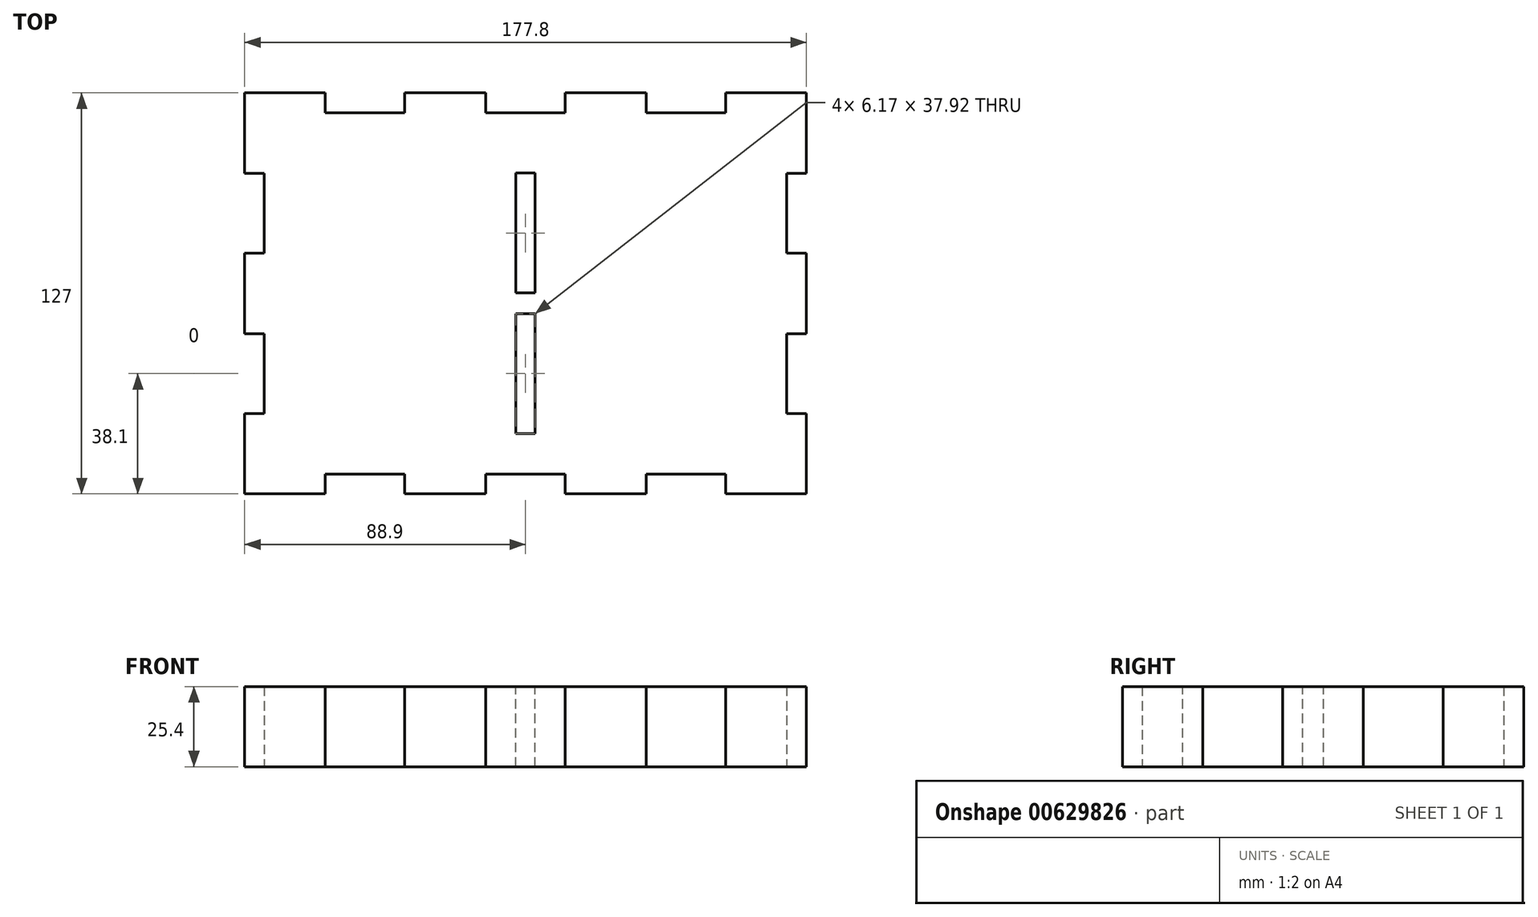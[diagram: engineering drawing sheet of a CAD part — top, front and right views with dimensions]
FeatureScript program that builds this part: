
annotation { "Feature Type Name" : "Feature", "Feature Type Description" : "" }
export const myFeature = defineFeature(function(context is Context, id is Id, definition is map)
    precondition{}
    {
        {
            var Q0;
            Q0=qCreatedBy(makeId("Top.planeOp"),FACE);
            var sketch = newSketch(context, id + "F0", { "sketchPlane" : qUnion([Q0])});
            skLineSegment(sketch, "E0.bottom", {"start": v(0, 0) * mm, "end": v(177.8, 0) * mm});
            skLineSegment(sketch, "E0.top", {"start": v(0, 127) * mm, "end": v(177.8, 127) * mm});
            skLineSegment(sketch, "E0.left", {"start": v(0, 0) * mm, "end": v(0, 127) * mm});
            skLineSegment(sketch, "E0.right", {"start": v(177.8, 0) * mm, "end": v(177.8, 127) * mm});
            skLineSegment(sketch, "E1.bottom", {"start": v(25.49, 0) * mm, "end": v(50.71, 0) * mm});
            skLineSegment(sketch, "E1.top", {"start": v(25.49, 6.26) * mm, "end": v(50.71, 6.26) * mm});
            skLineSegment(sketch, "E1.left", {"start": v(25.49, 0) * mm, "end": v(25.49, 6.26) * mm});
            skLineSegment(sketch, "E1.right", {"start": v(50.71, 0) * mm, "end": v(50.71, 6.26) * mm});
            skPoint(sketch, "E2", {"position": v(38.1, 6.26) * mm});
            skLineSegment(sketch, "E3.bottom", {"start": v(76.29, 6.26) * mm, "end": v(101.51, 6.26) * mm});
            skLineSegment(sketch, "E3.top", {"start": v(76.29, 0) * mm, "end": v(101.51, 0) * mm});
            skLineSegment(sketch, "E3.left", {"start": v(76.29, 6.26) * mm, "end": v(76.29, 0) * mm});
            skLineSegment(sketch, "E3.right", {"start": v(101.51, 6.26) * mm, "end": v(101.51, 0) * mm});
            skPoint(sketch, "E4", {"position": v(88.9, 6.26) * mm});
            skLineSegment(sketch, "E5.bottom", {"start": v(127.09, 6.26) * mm, "end": v(152.31, 6.26) * mm});
            skLineSegment(sketch, "E5.top", {"start": v(127.09, 0) * mm, "end": v(152.31, 0) * mm});
            skLineSegment(sketch, "E5.left", {"start": v(127.09, 6.26) * mm, "end": v(127.09, 0) * mm});
            skLineSegment(sketch, "E5.right", {"start": v(152.31, 6.26) * mm, "end": v(152.31, 0) * mm});
            skPoint(sketch, "E6", {"position": v(139.7, 6.26) * mm});
            skLineSegment(sketch, "E7.bottom", {"start": v(177.8, 25.49) * mm, "end": v(171.54, 25.49) * mm});
            skLineSegment(sketch, "E7.top", {"start": v(177.8, 50.71) * mm, "end": v(171.54, 50.71) * mm});
            skLineSegment(sketch, "E7.left", {"start": v(177.8, 25.49) * mm, "end": v(177.8, 50.71) * mm});
            skLineSegment(sketch, "E7.right", {"start": v(171.54, 25.49) * mm, "end": v(171.54, 50.71) * mm});
            skPoint(sketch, "E8", {"position": v(171.54, 38.1) * mm});
            skLineSegment(sketch, "E9.bottom", {"start": v(177.8, 101.51) * mm, "end": v(171.54, 101.51) * mm});
            skLineSegment(sketch, "E9.top", {"start": v(177.8, 76.29) * mm, "end": v(171.54, 76.29) * mm});
            skLineSegment(sketch, "E9.left", {"start": v(177.8, 101.51) * mm, "end": v(177.8, 76.29) * mm});
            skLineSegment(sketch, "E9.right", {"start": v(171.54, 101.51) * mm, "end": v(171.54, 76.29) * mm});
            skPoint(sketch, "E10", {"position": v(171.54, 88.9) * mm});
            skLineSegment(sketch, "E11", {"start": v(0, 63.5) * mm, "end": v(177.8, 63.5) * mm, "construction": true});
            skLineSegment(sketch, "E12.MirrorCS", {"start": v(25.49, 120.74) * mm, "end": v(50.71, 120.74) * mm});
            skLineSegment(sketch, "E13.MirrorCS", {"start": v(25.49, 127) * mm, "end": v(25.49, 120.74) * mm});
            skLineSegment(sketch, "E14.MirrorCS", {"start": v(50.71, 127) * mm, "end": v(50.71, 120.74) * mm});
            skLineSegment(sketch, "E15.MirrorCS", {"start": v(76.29, 120.74) * mm, "end": v(101.51, 120.74) * mm});
            skLineSegment(sketch, "E16.MirrorCS", {"start": v(76.29, 120.74) * mm, "end": v(76.29, 127) * mm});
            skLineSegment(sketch, "E17.MirrorCS", {"start": v(101.51, 120.74) * mm, "end": v(101.51, 127) * mm});
            skLineSegment(sketch, "E18.MirrorCS", {"start": v(127.09, 120.74) * mm, "end": v(127.09, 127) * mm});
            skLineSegment(sketch, "E19.MirrorCS", {"start": v(127.09, 120.74) * mm, "end": v(152.31, 120.74) * mm});
            skLineSegment(sketch, "E20.MirrorCS", {"start": v(152.31, 120.74) * mm, "end": v(152.31, 127) * mm});
            skLineSegment(sketch, "E21", {"start": v(88.9, 127) * mm, "end": v(88.9, 0) * mm, "construction": true});
            skLineSegment(sketch, "E22.MirrorCS", {"start": v(0, 101.51) * mm, "end": v(6.26, 101.51) * mm});
            skLineSegment(sketch, "E23.MirrorCS", {"start": v(6.26, 101.51) * mm, "end": v(6.26, 76.29) * mm});
            skLineSegment(sketch, "E24.MirrorCS", {"start": v(0, 76.29) * mm, "end": v(6.26, 76.29) * mm});
            skLineSegment(sketch, "E25.MirrorCS", {"start": v(0, 50.71) * mm, "end": v(6.26, 50.71) * mm});
            skLineSegment(sketch, "E26.MirrorCS", {"start": v(6.26, 25.49) * mm, "end": v(6.26, 50.71) * mm});
            skLineSegment(sketch, "E27.MirrorCS", {"start": v(0, 25.49) * mm, "end": v(6.26, 25.49) * mm});
            skSolve(sketch);
        }
        {
            var Q0;
            Q0=makeQuery(id+"F0.imprint","IMPRINT",FACE,{"disambiguationData":[TD([[makeQuery(id+"F0.imprint","IMPRINT",EDGE,{"derivedFrom":sQuery(id+"F0.wireOp",EDGE,"E1.top")}),1.0]])]});
            extrude(context, id + "F1", {"entities" : qUnion([Q0]), "depth" : 25.4 * mm, "offsetDistance" : 25.4 * mm});
        }
        {
            var Q0;
            Q0=makeQuery(id+"F1.opExtrude","CAP_FACE",FACE,{"disambiguationData":[OSD([sQuery(id+"F0.wireOp",EDGE,"E0.bottom"),sQuery(id+"F0.wireOp",EDGE,"E0.top"),sQuery(id+"F0.wireOp",EDGE,"E0.left"),sQuery(id+"F0.wireOp",EDGE,"E0.right"),sQuery(id+"F0.wireOp",EDGE,"E1.top"),sQuery(id+"F0.wireOp",EDGE,"E1.left"),sQuery(id+"F0.wireOp",EDGE,"E1.right"),sQuery(id+"F0.wireOp",EDGE,"E3.bottom"),sQuery(id+"F0.wireOp",EDGE,"E3.left"),sQuery(id+"F0.wireOp",EDGE,"E3.right"),sQuery(id+"F0.wireOp",EDGE,"E5.bottom"),sQuery(id+"F0.wireOp",EDGE,"E5.left"),sQuery(id+"F0.wireOp",EDGE,"E5.right"),sQuery(id+"F0.wireOp",EDGE,"E7.bottom"),sQuery(id+"F0.wireOp",EDGE,"E7.top"),sQuery(id+"F0.wireOp",EDGE,"E7.right"),sQuery(id+"F0.wireOp",EDGE,"E9.bottom"),sQuery(id+"F0.wireOp",EDGE,"E9.top"),sQuery(id+"F0.wireOp",EDGE,"E9.right"),sQuery(id+"F0.wireOp",EDGE,"E12.MirrorCS"),sQuery(id+"F0.wireOp",EDGE,"E13.MirrorCS"),sQuery(id+"F0.wireOp",EDGE,"E14.MirrorCS"),sQuery(id+"F0.wireOp",EDGE,"E15.MirrorCS"),sQuery(id+"F0.wireOp",EDGE,"E16.MirrorCS"),sQuery(id+"F0.wireOp",EDGE,"E17.MirrorCS"),sQuery(id+"F0.wireOp",EDGE,"E18.MirrorCS"),sQuery(id+"F0.wireOp",EDGE,"E19.MirrorCS"),sQuery(id+"F0.wireOp",EDGE,"E20.MirrorCS"),sQuery(id+"F0.wireOp",EDGE,"E22.MirrorCS"),sQuery(id+"F0.wireOp",EDGE,"E23.MirrorCS"),sQuery(id+"F0.wireOp",EDGE,"E24.MirrorCS"),sQuery(id+"F0.wireOp",EDGE,"E25.MirrorCS"),sQuery(id+"F0.wireOp",EDGE,"E26.MirrorCS"),sQuery(id+"F0.wireOp",EDGE,"E27.MirrorCS")])],"isStart":false});
            var sketch = newSketch(context, id + "F2", { "sketchPlane" : qUnion([Q0])});
            skLineSegment(sketch, "E28.bottom", {"start": v(85.81, 101.6) * mm, "end": v(91.99, 101.6) * mm});
            skLineSegment(sketch, "E28.top", {"start": v(85.81, 63.68) * mm, "end": v(91.99, 63.68) * mm});
            skLineSegment(sketch, "E28.left", {"start": v(85.81, 101.6) * mm, "end": v(85.81, 63.68) * mm});
            skLineSegment(sketch, "E28.right", {"start": v(91.99, 101.6) * mm, "end": v(91.99, 63.68) * mm});
            skPoint(sketch, "E29", {"position": v(91.99, 82.64) * mm});
            skPoint(sketch, "E30", {"position": v(88.9, 120.74) * mm});
            skPoint(sketch, "E31", {"position": v(88.9, 6.26) * mm});
            skLineSegment(sketch, "E32.bottom", {"start": v(85.81, 57.06) * mm, "end": v(91.99, 57.06) * mm});
            skLineSegment(sketch, "E32.top", {"start": v(85.81, 19.14) * mm, "end": v(91.99, 19.14) * mm});
            skLineSegment(sketch, "E32.left", {"start": v(85.81, 57.06) * mm, "end": v(85.81, 19.14) * mm});
            skLineSegment(sketch, "E32.right", {"start": v(91.99, 57.06) * mm, "end": v(91.99, 19.14) * mm});
            skPoint(sketch, "E33", {"position": v(88.9, 57.06) * mm});
            skPoint(sketch, "E34", {"position": v(85.81, 38.1) * mm});
            skSolve(sketch);
        }
        {
            var Q0;
            Q0=makeQuery(id+"F2.imprint","IMPRINT",FACE,{"disambiguationData":[TD([[makeQuery(id+"F2.imprint","IMPRINT",EDGE,{"derivedFrom":sQuery(id+"F2.wireOp",EDGE,"E28.bottom")}),-1.0]])]});
            var Q1;
            Q1=makeQuery(id+"F2.imprint","IMPRINT",FACE,{"disambiguationData":[TD([[makeQuery(id+"F2.imprint","IMPRINT",EDGE,{"derivedFrom":sQuery(id+"F2.wireOp",EDGE,"E32.bottom")}),-1.0]])]});
            extrude(context, id + "F3", {"entities" : qUnion([Q0, Q1]), "operationType" : NewBodyOperationType.REMOVE, "endBound" : BoundingType.THROUGH_ALL, "oppositeDirection" : true, "depth" : 25.4 * mm, "offsetDistance" : 25.4 * mm});
        }
    });
